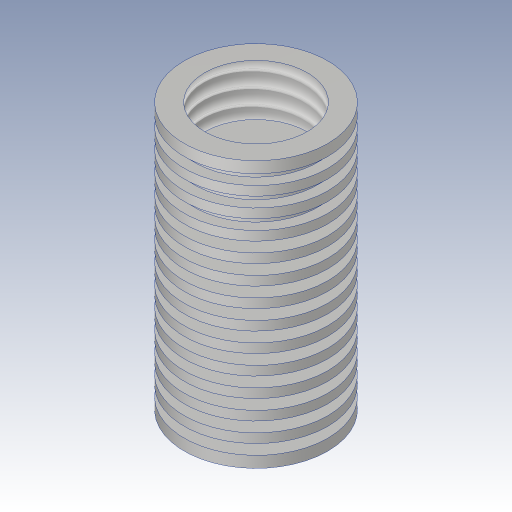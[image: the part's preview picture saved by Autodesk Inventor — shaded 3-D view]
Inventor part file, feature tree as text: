
AUTODESK INVENTOR PART (.ipt)
format: ipt  version: 2023.3 (Build 273359000, 359)  size: 329,216 bytes
history: native  units: in
note: dims shown in document units (in); Inventor stores cm internally (conversion verified against a paired STEP export)
features: revolve x2, thread x2, sketch x2
ambient origin geometry x8: Origin, YZ Plane, XZ Plane, XY Plane, X Axis, Y Axis, Z Axis, Center Point
bodies: Body1 (feature_tree)
feature tree (6):
  revolve  "Umdrehung1"
  thread  "Gewinde1"  [1 undecoded]
  thread  "Gewinde2"  [1 undecoded]
  revolve  "Umdrehung2"
  sketch  "Skizze3"  dims[d7=0.2362in]
  sketch  "Skizze4"  dims[d8=0.0787in d9=0.5512in d10=1.0236in d11=0.3937in d12=0.1969in d13=0.1654in d14=90.0deg d15=0.1969in d16=0.0394in d17=0.1969in d18=0.0in d21=0.0394in d22=0.0709in d23=2.7559in d25=0.0748in d26=0.3937in d28=0.3937in d31=0.0394in d32=0.0433in d33=1.1811in d35=0.0748in d36=0.3937in d38=0.3937in d41=0.0394in d42=0.0354in d43=1.1811in d45=0.0748in d46=0.3937in d48=0.3937in d50=360.0deg d51=0.0394in d52=0.0551in d53=0.0394in]
note: 2 required parameter values undecoded (feature->parameter linkage not recoverable at this tier; creation-order binding heuristic only, values carry confidence <= 0.55)
